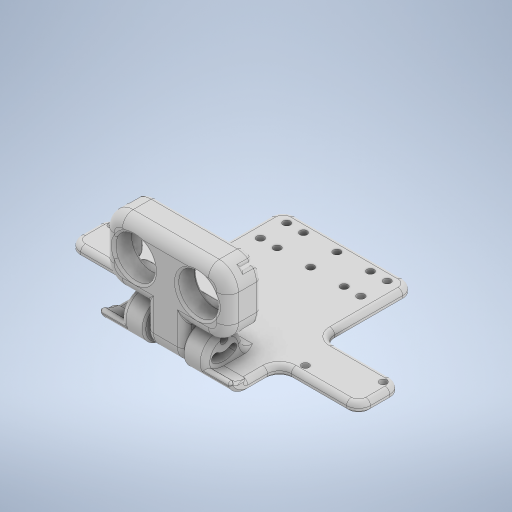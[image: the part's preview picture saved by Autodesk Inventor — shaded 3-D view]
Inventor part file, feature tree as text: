
AUTODESK INVENTOR PART (.ipt)
format: ipt  version: 2023 (Build 270158030, 158C)  size: 1,454,592 bytes
history: native  units: mm
features: fillet x26, extrude x20, sketch x19, projected_geometry x5, other x3, chamfer x3, mirror x2, plane x1
ambient origin geometry x8: Origin, YZ Plane, XZ Plane, XY Plane, X Axis, Y Axis, Z Axis, Center Point
bodies: Body1 (feature_tree), Body2 (feature_tree), Body3 (feature_tree)
feature tree (79):
  other  "Ping Sensor Base"
  extrude  "Extrusion1"  Depth=3.0mm TaperAngle=0.0deg
  extrude  "Extrusion2"  Depth=3.0mm TaperAngle=0.0deg
  extrude  "Extrusion3"  Depth=1.55mm
  fillet  "Fillet1"  Radius=12.0mm
  extrude  "Extrusion4"  Depth=14.0mm
  extrude  "Extrusion6"  Depth=1.5mm
  fillet  "Fillet9"  Radius=7.0mm
  fillet  "Fillet10"  Radius=7.0mm
  fillet  "Fillet11"  [1 undecoded]
  fillet  "Fillet12"  Radius=15.0mm
  fillet  "Fillet15"  Radius=6.0mm
  fillet  "Fillet16"  Radius=15.0mm
  extrude  "Extrusion7"  Depth=30.0mm
  extrude  "Extrusion8"  Depth=3.1mm
  extrude  "Extrusion9"  Depth=3.0mm
  extrude  "Extrusion10"  Depth=8.2mm
  fillet  "Fillet17"  Radius=10.2mm
  fillet  "Fillet18"  Radius=8.2mm
  fillet  "Fillet19"  Radius=10.2mm
  fillet  "Fillet20"  Radius=7.5mm
  fillet  "Fillet21"  Radius=7.5mm
  fillet  "Fillet22"  [1 undecoded]
  extrude  "Extrusion11"  Depth=7.0mm
  fillet  "Fillet27"  Radius=2.0mm
  extrude  "Extrusion13"  Depth=2.0mm
  fillet  "Fillet29"  Radius=3.0mm
  fillet  "Fillet30"  Radius=17.0mm
  fillet  "Fillet31"  Radius=26.0mm
  fillet  "Fillet32"  Radius=10.0mm
  fillet  "Fillet33"  Radius=27.0mm
  extrude  "Extrusion14"  Depth=26.0mm
  mirror  "Mirror1"
  extrude  "Extrusion15"  Depth=45.8mm
  fillet  "Fillet34"  Radius=20.8mm
  extrude  "Extrusion17"  Depth=3.1mm
  mirror  "Mirror2"
  fillet  "Fillet35"  Radius=3.1mm
  fillet  "Fillet36"  Radius=3.1mm
  fillet  "Fillet39"  Radius=5.5mm
  plane  "Work Plane4"
  extrude  "Extrusion18"  Depth=17.0mm
  extrude  "Extrusion19"  Depth=9.75mm
  chamfer  "Chamfer1"  Distance=9.3mm
  chamfer  "Chamfer2"  [1 undecoded]
  fillet  "Fillet40"  Radius=8.0mm
  extrude  "Extrusion20"  Depth=4.5mm
  extrude  "Extrusion21"  Depth=2.0mm
  extrude  "Extrusion22"  Depth=7.0mm
  extrude  "Extrusion23"  Depth=3.0mm
  fillet  "Fillet41"  Radius=1.0mm
  chamfer  "Chamfer4"  Distance=3.1mm
  fillet  "Fillet42"  Radius=3.1mm
  sketch  "Sketch1"  dims[d0=36.0mm d1=3.0mm d2=0.0mm]
  sketch  "Sketch2"  dims[d3=3.1mm d4=3.0mm d5=0.0mm]
  sketch  "Sketch3"  dims[d7=3.1mm d8=1.55mm d9=12.0mm]
  sketch  "Sketch4"  dims[d10=3.0mm d11=0.0mm d15=14.0mm]
  sketch  "Sketch6"  dims[d16=3.5mm d17=1.5mm]
  sketch  "Sketch7"  dims[d18=2.5mm d19=6.5mm d20=20.0mm d21=0.0mm d22=7.0mm d23=7.0mm d24=0.0mm d25=15.0mm d37=6.0mm d54=15.0mm]
  other  "Ping Sensor Housing"
  sketch  "Sketch8"  dims[d55=15.0mm d56=30.0mm]
  sketch  "Sketch9"  dims[d57=3.0mm d58=3.1mm]
  sketch  "Sketch10"  dims[d59=4.5mm d60=3.0mm]
  sketch  "Sketch11"  dims[d61=3.1mm d62=8.2mm d63=10.2mm d64=8.2mm d65=10.2mm d66=7.5mm d67=7.5mm d68=0.0mm d69=0.0mm]
  sketch  "Sketch13"  dims[d70=1.5mm d71=7.0mm d72=2.0mm]
  sketch  "Sketch14"  dims[d73=1.0mm d76=2.0mm d77=3.0mm d78=17.0mm d79=26.0mm d80=10.0mm d81=0.0mm d82=27.0mm]
  projected_geometry  "Projected Loop1"
  projected_geometry  "Projected Loop2"
  other  "hoz-mount"
  sketch  "Sketch15"  dims[d83=26.0mm d84=26.0mm]
  projected_geometry  "Projected Loop3"
  sketch  "Sketch17"  dims[d85=10.0mm d86=0.0mm d87=45.8mm d88=20.8mm]
  projected_geometry  "Projected Loop7"
  sketch  "Sketch19"  dims[d89=3.1mm d90=3.1mm d91=3.1mm d92=3.1mm d93=5.5mm d94=0.0mm]
  sketch  "Sketch20"  dims[d95=17.0mm d96=17.0mm]
  sketch  "Sketch21"  dims[d97=9.75mm d99=9.75mm]
  sketch  "Sketch22"  dims[d100=10.0mm]
  sketch  "Sketch23"  dims[d101=10.0mm d102=9.3mm d103=0.0mm d104=0.0mm d105=8.0mm d106=4.5mm d107=2.0mm d108=7.0mm d109=3.0mm d110=1.0mm d111=3.1mm d112=3.1mm d113=6.1mm d114=0.0mm d115=0.0mm d116=4.0mm d118=4.0mm d135=0.9mm d137=0.0mm d138=6.0mm d139=5.0mm d140=5.0mm d141=4.0mm d142=3.0mm d143=0.0mm d144=1.0mm d145=0.3mm d146=1.0mm d147=26.3mm d148=43.3mm d149=1.0mm d150=1.0mm d160=1.0mm d161=67.7mm d162=4.0mm d163=6.0mm d164=3.5mm d165=3.5mm d166=0.1mm d167=0.2mm d168=19.5mm d169=0.0mm d170=10.0mm d171=0.0mm d172=2.0mm d177=10.0mm d178=0.0mm d179=2.0mm d180=1.0mm d183=2.0mm d185=42.0mm d188=3.1mm d189=0.0mm d190=0.0mm d191=4.75mm d192=4.0mm d193=0.0mm d194=2.0mm d195=2.0mm d196=45.0deg d197=0.8mm d198=2.0mm d199=45.0deg d203=0.3mm d204=33.1mm d205=33.1mm d206=20.47mm d208=10.0mm d209=0.0mm d210=3.0mm d211=10.3mm d212=22.2mm d213=22.2mm d214=3.9mm d215=3.877918mm d216=3.9mm d217=3.9mm d218=0.0mm d219=0.0mm d220=3.0mm d223=27.5mm d224=55.0mm d225=14.0mm d226=14.0mm d227=6.5mm d228=6.5mm d229=28.49mm d230=6.0mm d231=0.0mm d232=0.0mm d233=10.0mm d234=5.0mm d235=10.0mm d236=0.0mm d237=5.0mm d238=1.0mm d239=2.0mm d240=45.0deg d241=2.0mm]
  projected_geometry  "Projected Loop8"
note: 3 required parameter values undecoded (feature->parameter linkage not recoverable at this tier; creation-order binding heuristic only, values carry confidence <= 0.55)
